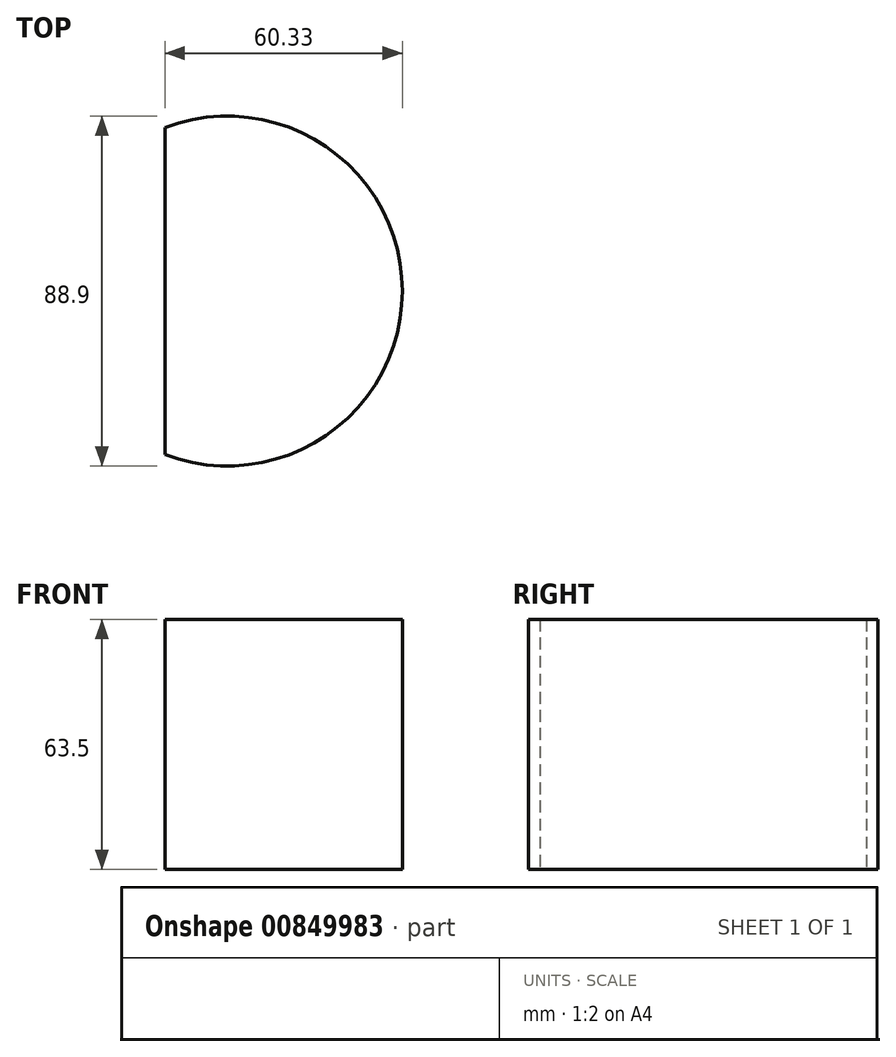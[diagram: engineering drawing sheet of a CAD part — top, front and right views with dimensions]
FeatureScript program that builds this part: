
annotation { "Feature Type Name" : "Feature", "Feature Type Description" : "" }
export const myFeature = defineFeature(function(context is Context, id is Id, definition is map)
    precondition{}
    {
        {
            var Q0;
            Q0=qCreatedBy(makeId("Top.planeOp"),FACE);
            var sketch = newSketch(context, id + "F0", { "sketchPlane" : qUnion([Q0])});
            skArc(sketch, "E0", {"start": v(-15.88, -41.52) * mm, "mid": v(44.45, 0) * mm, "end": v(-15.87, 41.52) * mm});
            skLineSegment(sketch, "E1", {"start": v(-15.88, 41.52) * mm, "end": v(-15.87, -41.52) * mm});
            skSolve(sketch);
        }
        {
            var Q0;
            Q0 = qSketchRegion(id + "F0", true);
            extrude(context, id + "F1", {"entities" : qUnion([Q0]), "depth" : 63.5 * mm, "offsetDistance" : 25.4 * mm});
        }
    });
